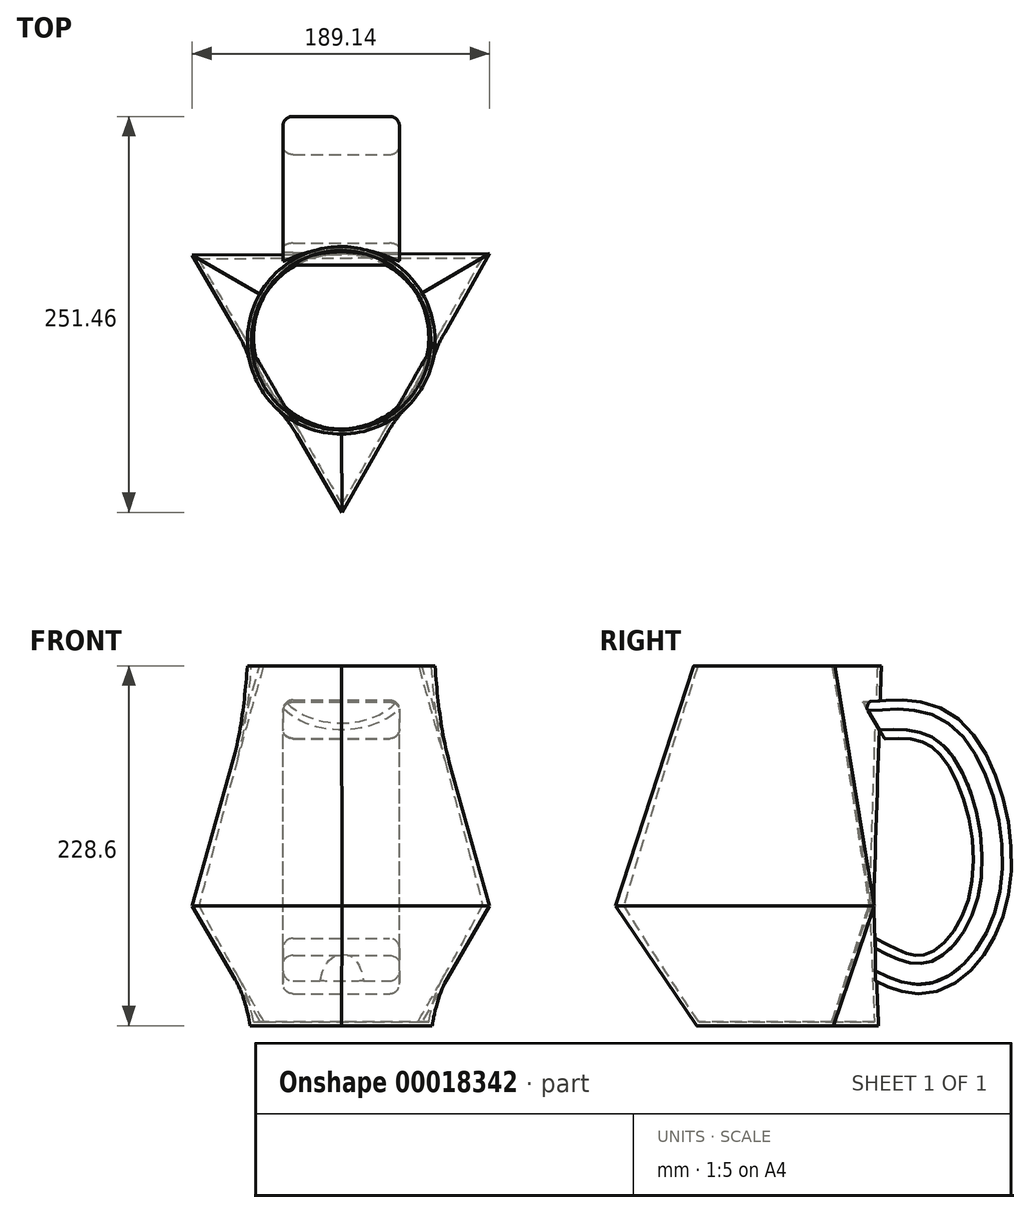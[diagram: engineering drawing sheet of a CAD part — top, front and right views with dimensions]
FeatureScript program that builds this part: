
annotation { "Feature Type Name" : "Feature", "Feature Type Description" : "" }
export const myFeature = defineFeature(function(context is Context, id is Id, definition is map)
    precondition{}
    {
        {
            var Q0;
            Q0=qCreatedBy(makeId("Top.planeOp"),FACE);
            cPlane(context, id + "F0", {"entities" : qUnion([Q0]), "cplaneType" : CPlaneType.OFFSET, "offset" : 76.2 * mm, "width" : 152.4 * mm, "height" : 152.4 * mm});
        }
        {
            var Q0;
            Q0=qCreatedBy(id+"F0.planeOp",FACE);
            var sketch = newSketch(context, id + "F1", { "sketchPlane" : qUnion([Q0])});
            skCircle(sketch, "E0.cCircle", {"center": v(0, 0) * mm, "radius": 54.6 * mm, "construction": true});
            skLineSegment(sketch, "E0.0", {"start": v(94.3, 55.05) * mm, "end": v(0.52, -109.2) * mm});
            skLineSegment(sketch, "E0.1", {"start": v(0.52, -109.2) * mm, "end": v(-94.83, 54.15) * mm});
            skLineSegment(sketch, "E0.2", {"start": v(-94.83, 54.15) * mm, "end": v(94.3, 55.05) * mm});
            skPoint(sketch, "E0.0.midPoint", {"position": v(47.42, -27.07) * mm});
            skSolve(sketch);
        }
        {
            var Q0;
            Q0=qCreatedBy(makeId("Top.planeOp"),FACE);
            var sketch = newSketch(context, id + "F2", { "sketchPlane" : qUnion([Q0])});
            skCircle(sketch, "E1", {"center": v(0, 0) * mm, "radius": 57.76 * mm});
            skSolve(sketch);
        }
        {
            var Q0;
            Q0=makeQuery(id+"F1.imprint","IMPRINT",FACE,{"disambiguationData":[TD([[makeQuery(id+"F1.imprint","IMPRINT",EDGE,{"derivedFrom":sQuery(id+"F1.wireOp",EDGE,"E0.0")}),-1.0]])]});
            var Q1;
            Q1=makeQuery(id+"F2.imprint","IMPRINT",FACE,{"disambiguationData":[TD([[makeQuery(id+"F2.imprint","IMPRINT",EDGE,{"derivedFrom":sQuery(id+"F2.wireOp",EDGE,"E1")}),1.0]])]});
            loft(context, id + "F3", {"sheetProfilesArray" : [{ "sheetProfileEntities" : qUnion([Q0]) }, { "sheetProfileEntities" : qUnion([Q1]) }]});
        }
        {
            var Q0;
            Q0=qCreatedBy(id+"F0.planeOp",FACE);
            cPlane(context, id + "F4", {"entities" : qUnion([Q0]), "cplaneType" : CPlaneType.OFFSET, "offset" : 152.4 * mm, "width" : 152.4 * mm, "height" : 152.4 * mm});
        }
        {
            var Q0;
            Q0=qCreatedBy(id+"F4.planeOp",FACE);
            var sketch = newSketch(context, id + "F5", { "sketchPlane" : qUnion([Q0])});
            skPoint(sketch, "E2.0", {"position": v(0, 0) * mm});
            skCircle(sketch, "E3", {"center": v(0, 0) * mm, "radius": 59.54 * mm});
            skSolve(sketch);
        }
        {
            var Q1;
            Q1=makeQuery(id+"F3.opLoft","CAP_FACE",FACE,{"disambiguationData":[OSD([makeQuery(id+"F1.imprint","IMPRINT",FACE,{"disambiguationData":[TD([[makeQuery(id+"F1.imprint","IMPRINT",EDGE,{"derivedFrom":sQuery(id+"F1.wireOp",EDGE,"E0.0")}),-1.0]])]})])],"isStart":true});
            var Q2;
            Q2=makeQuery(id+"F5.imprint","IMPRINT",FACE,{"disambiguationData":[TD([[makeQuery(id+"F5.imprint","IMPRINT",EDGE,{"derivedFrom":sQuery(id+"F5.wireOp",EDGE,"E3")}),1.0]])]});
            loft(context, id + "F6", {"operationType" : NewBodyOperationType.ADD, "sheetProfilesArray" : [{ "sheetProfileEntities" : qUnion([Q1]) }, { "sheetProfileEntities" : qUnion([Q2]) }]});
        }
        {
            var Q0;
            Q0=makeQuery(id+"F6.opLoft","CAP_FACE",FACE,{"disambiguationData":[OSD([makeQuery(id+"F5.imprint","IMPRINT",FACE,{"disambiguationData":[TD([[makeQuery(id+"F5.imprint","IMPRINT",EDGE,{"derivedFrom":sQuery(id+"F5.wireOp",EDGE,"E3")}),1.0]])]})])],"isStart":true});
            shell(context, id + "F7", {"entities" : qUnion([Q0]), "thickness" : 2.54 * mm});
        }
        {
            var Q0;
            Q0=qCreatedBy(makeId("Front.planeOp"),FACE);
            cPlane(context, id + "F8", {"entities" : qUnion([Q0]), "cplaneType" : CPlaneType.OFFSET, "offset" : 55.88 * mm, "oppositeDirection" : true, "width" : 152.4 * mm, "height" : 152.4 * mm});
        }
        {
            var Q0;
            Q0=qCreatedBy(id+"F8.planeOp",FACE);
            var sketch = newSketch(context, id + "F9", { "sketchPlane" : qUnion([Q0])});
            skLineSegment(sketch, "E4.rect.bottom", {"start": v(-30.58, 28.41) * mm, "end": v(30.58, 28.41) * mm});
            skLineSegment(sketch, "E4.rect.top", {"start": v(-30.58, 55.49) * mm, "end": v(30.58, 55.49) * mm});
            skLineSegment(sketch, "E4.rect.left", {"start": v(-36.93, 34.76) * mm, "end": v(-36.93, 49.14) * mm});
            skLineSegment(sketch, "E4.rect.right", {"start": v(36.93, 34.76) * mm, "end": v(36.93, 49.14) * mm});
            skPoint(sketch, "E4.rect.middle", {"position": v(0, 41.95) * mm});
            skPoint(sketch, "E5.visualSharp", {"position": v(36.93, 55.49) * mm});
            skArc(sketch, "E5.filletArc", {"start": v(36.93, 49.14) * mm, "mid": v(35.07, 53.63) * mm, "end": v(30.58, 55.49) * mm});
            skPoint(sketch, "E6.visualSharp", {"position": v(-36.93, 55.49) * mm});
            skArc(sketch, "E6.filletArc", {"start": v(-30.58, 55.49) * mm, "mid": v(-35.07, 53.63) * mm, "end": v(-36.93, 49.14) * mm});
            skPoint(sketch, "E7.visualSharp", {"position": v(-36.93, 28.41) * mm});
            skArc(sketch, "E7.filletArc", {"start": v(-36.93, 34.76) * mm, "mid": v(-35.07, 30.27) * mm, "end": v(-30.58, 28.41) * mm});
            skPoint(sketch, "E8.visualSharp", {"position": v(36.93, 28.41) * mm});
            skArc(sketch, "E8.filletArc", {"start": v(30.58, 28.41) * mm, "mid": v(35.07, 30.27) * mm, "end": v(36.93, 34.76) * mm});
            skSolve(sketch);
        }
        {
            var Q0;
            Q0=qCreatedBy(makeId("Right.planeOp"),FACE);
            var sketch = newSketch(context, id + "F10", { "sketchPlane" : qUnion([Q0])});
            skFitSpline(sketch, "E9", {"points": [v(56.2, 47.06) * mm, v(89.9, 38.64) * mm, v(124.07, 88.71) * mm, v(99.26, 179.97) * mm, v(57.14, 189.33) * mm], "startDerivative": vector(170.86, -88.4) * mm, "endDerivative": vector(-204.9, -11.45) * mm});
            skSolve(sketch);
        }
        {
            var Q0;
            Q0=makeQuery(id+"F9.imprint","IMPRINT",FACE,{"disambiguationData":[TD([[makeQuery(id+"F9.imprint","IMPRINT",EDGE,{"derivedFrom":sQuery(id+"F9.wireOp",EDGE,"E4.rect.bottom")}),1.0]])]});
            var Q1;
            Q1=sQuery(id+"F10.wireOp",EDGE,"E9");
            sweep(context, id + "F11", {"operationType" : NewBodyOperationType.ADD, "profiles" : qUnion([Q0]), "path" : qUnion([Q1])});
        }
    });
